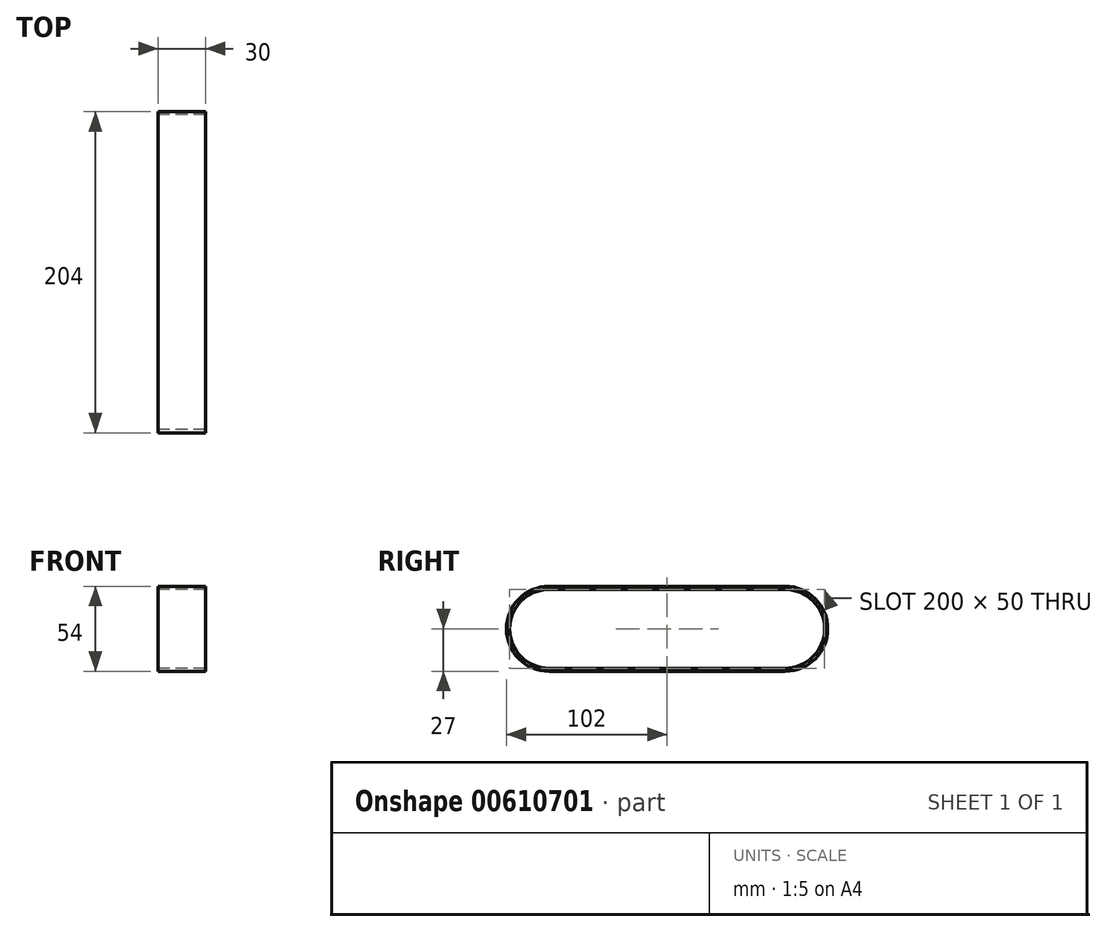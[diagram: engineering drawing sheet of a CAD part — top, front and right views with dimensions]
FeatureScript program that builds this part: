
annotation { "Feature Type Name" : "Feature", "Feature Type Description" : "" }
export const myFeature = defineFeature(function(context is Context, id is Id, definition is map)
    precondition{}
    {
        {
            var Q0;
            Q0=qCreatedBy(makeId("Right.planeOp"),FACE);
            var sketch = newSketch(context, id + "F0", { "sketchPlane" : qUnion([Q0])});
            skArc(sketch, "E0", {"start": v(0, 25) * mm, "mid": v(-25, 0) * mm, "end": v(0, -25) * mm});
            skArc(sketch, "E1", {"start": v(150, -25) * mm, "mid": v(175, 0) * mm, "end": v(150, 25) * mm});
            skLineSegment(sketch, "E2", {"start": v(150, -25) * mm, "end": v(0, -25) * mm});
            skLineSegment(sketch, "E3", {"start": v(0, 25) * mm, "end": v(150, 25) * mm});
            skArc(sketch, "E4.0", {"start": v(0, 27) * mm, "mid": v(-27, 0) * mm, "end": v(0, -27) * mm});
            skLineSegment(sketch, "E4.1", {"start": v(0, 27) * mm, "end": v(150, 27) * mm});
            skArc(sketch, "E4.2", {"start": v(150, -27) * mm, "mid": v(177, 0) * mm, "end": v(150, 27) * mm});
            skLineSegment(sketch, "E4.3", {"start": v(150, -27) * mm, "end": v(0, -27) * mm});
            skSolve(sketch);
        }
        {
            var Q0;
            Q0 = qSketchRegion(id + "F0", true);
            extrude(context, id + "F1", {"entities" : qUnion([Q0]), "depth" : 30 * mm, "offsetDistance" : 25 * mm});
        }
    });
